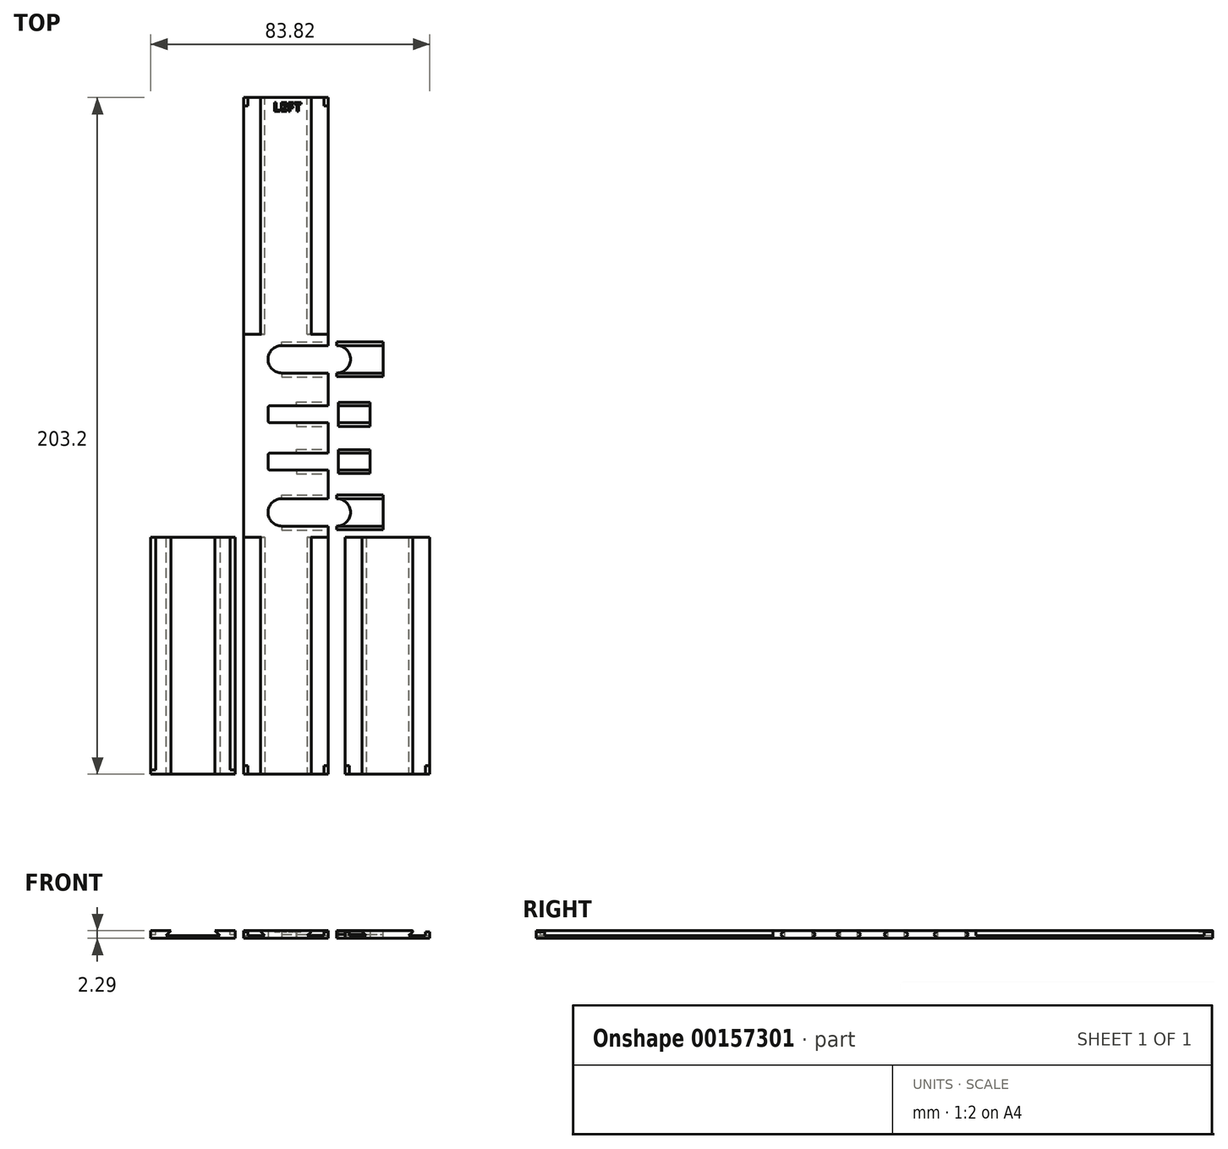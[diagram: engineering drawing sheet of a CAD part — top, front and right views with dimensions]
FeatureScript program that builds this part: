
annotation { "Feature Type Name" : "Feature", "Feature Type Description" : "" }
export const myFeature = defineFeature(function(context is Context, id is Id, definition is map)
    precondition{}
    {
        {
            var Q0;
            Q0=qCreatedBy(makeId("Top.planeOp"),FACE);
            var sketch = newSketch(context, id + "F0", { "sketchPlane" : qUnion([Q0])});
            skLineSegment(sketch, "E0.bottom", {"start": v(-2.54, 205.74) * mm, "end": v(-27.94, 205.74) * mm});
            skLineSegment(sketch, "E0.top", {"start": v(-2.54, 2.54) * mm, "end": v(-27.94, 2.54) * mm});
            skLineSegment(sketch, "E0.left", {"start": v(-2.54, 205.74) * mm, "end": v(-2.54, 131.27) * mm});
            skLineSegment(sketch, "E0.right", {"start": v(-27.94, 205.74) * mm, "end": v(-27.94, 2.54) * mm});
            skLineSegment(sketch, "E1.bottom", {"start": v(-30.48, 2.54) * mm, "end": v(-55.88, 2.54) * mm});
            skLineSegment(sketch, "E1.top", {"start": v(-30.48, 73.66) * mm, "end": v(-55.88, 73.66) * mm});
            skLineSegment(sketch, "E1.left", {"start": v(-30.48, 2.54) * mm, "end": v(-30.48, 73.66) * mm});
            skLineSegment(sketch, "E1.right", {"start": v(-55.88, 2.54) * mm, "end": v(-55.88, 73.66) * mm});
            skLineSegment(sketch, "E2.MirrorCS", {"start": v(2.54, 2.54) * mm, "end": v(2.54, 73.66) * mm});
            skLineSegment(sketch, "E3.MirrorCS", {"start": v(2.54, 73.66) * mm, "end": v(27.94, 73.66) * mm});
            skLineSegment(sketch, "E4.MirrorCS", {"start": v(27.94, 2.54) * mm, "end": v(27.94, 73.66) * mm});
            skLineSegment(sketch, "E5.MirrorCS", {"start": v(2.54, 2.54) * mm, "end": v(27.94, 2.54) * mm});
            skPoint(sketch, "E6.MirrorCS.start.orphan", {"position": v(-30.48, 73.66) * mm});
            skArc(sketch, "E7", {"start": v(-16.51, 131.27) * mm, "mid": v(-20.64, 127.14) * mm, "end": v(-16.51, 123.01) * mm});
            skArc(sketch, "E8", {"start": v(-16.51, 85.3) * mm, "mid": v(-20.64, 81.17) * mm, "end": v(-16.51, 77.04) * mm});
            skLineSegment(sketch, "E9", {"start": v(-16.51, 131.27) * mm, "end": v(-2.54, 131.27) * mm});
            skLineSegment(sketch, "E10", {"start": v(-16.51, 123.01) * mm, "end": v(-2.54, 123.01) * mm});
            skLineSegment(sketch, "E11", {"start": v(-16.51, 85.3) * mm, "end": v(-2.54, 85.3) * mm});
            skLineSegment(sketch, "E12", {"start": v(-16.51, 77.04) * mm, "end": v(-2.54, 77.04) * mm});
            skLineSegment(sketch, "E13.bottom", {"start": v(0, 77.04) * mm, "end": v(13.97, 77.04) * mm});
            skLineSegment(sketch, "E13.top", {"start": v(0, 85.3) * mm, "end": v(13.97, 85.3) * mm});
            skLineSegment(sketch, "E13.right", {"start": v(13.97, 77.04) * mm, "end": v(13.97, 85.3) * mm});
            skLineSegment(sketch, "E14.bottom", {"start": v(0, 123.01) * mm, "end": v(13.97, 123.01) * mm});
            skLineSegment(sketch, "E14.top", {"start": v(0, 131.27) * mm, "end": v(13.97, 131.27) * mm});
            skLineSegment(sketch, "E14.right", {"start": v(13.97, 123.01) * mm, "end": v(13.97, 131.27) * mm});
            skArc(sketch, "E15", {"start": v(0, 77.04) * mm, "mid": v(4.13, 81.17) * mm, "end": v(0, 85.3) * mm});
            skArc(sketch, "E16", {"start": v(0, 123.01) * mm, "mid": v(4.13, 127.14) * mm, "end": v(0, 131.27) * mm});
            skLineSegment(sketch, "E17.bottom", {"start": v(-2.54, 93.87) * mm, "end": v(-20.13, 93.87) * mm});
            skLineSegment(sketch, "E17.top", {"start": v(-2.54, 98.95) * mm, "end": v(-20.13, 98.95) * mm});
            skLineSegment(sketch, "E17.right", {"start": v(-20.64, 94.37) * mm, "end": v(-20.64, 98.44) * mm});
            skLineSegment(sketch, "E18.bottom", {"start": v(-2.54, 108.09) * mm, "end": v(-20.13, 108.09) * mm});
            skLineSegment(sketch, "E18.top", {"start": v(-2.54, 113.17) * mm, "end": v(-20.13, 113.17) * mm});
            skLineSegment(sketch, "E18.right", {"start": v(-20.64, 108.6) * mm, "end": v(-20.64, 112.66) * mm});
            skPoint(sketch, "E19.visualSharp", {"position": v(-20.64, 113.17) * mm});
            skArc(sketch, "E19.filletArc", {"start": v(-20.13, 113.17) * mm, "mid": v(-20.49, 113.02) * mm, "end": v(-20.64, 112.66) * mm});
            skPoint(sketch, "E20.visualSharp", {"position": v(-20.64, 108.09) * mm});
            skArc(sketch, "E20.filletArc", {"start": v(-20.64, 108.6) * mm, "mid": v(-20.49, 108.24) * mm, "end": v(-20.13, 108.09) * mm});
            skPoint(sketch, "E21.visualSharp", {"position": v(-20.64, 98.95) * mm});
            skArc(sketch, "E21.filletArc", {"start": v(-20.13, 98.95) * mm, "mid": v(-20.49, 98.8) * mm, "end": v(-20.64, 98.44) * mm});
            skPoint(sketch, "E22.visualSharp", {"position": v(-20.64, 93.87) * mm});
            skArc(sketch, "E22.filletArc", {"start": v(-20.64, 94.37) * mm, "mid": v(-20.49, 94.01) * mm, "end": v(-20.13, 93.87) * mm});
            skLineSegment(sketch, "E23.bottom", {"start": v(0.42, 113.17) * mm, "end": v(9.95, 113.17) * mm});
            skLineSegment(sketch, "E23.top", {"start": v(0.42, 108.09) * mm, "end": v(9.95, 108.09) * mm});
            skLineSegment(sketch, "E23.left", {"start": v(0.42, 113.17) * mm, "end": v(0.42, 108.09) * mm});
            skLineSegment(sketch, "E23.right", {"start": v(9.95, 113.17) * mm, "end": v(9.95, 108.09) * mm});
            skLineSegment(sketch, "E24.bottom", {"start": v(0.42, 98.95) * mm, "end": v(9.95, 98.95) * mm});
            skLineSegment(sketch, "E24.top", {"start": v(0.42, 93.9) * mm, "end": v(9.95, 93.9) * mm});
            skLineSegment(sketch, "E24.left", {"start": v(0.42, 98.95) * mm, "end": v(0.42, 93.9) * mm});
            skLineSegment(sketch, "E24.right", {"start": v(9.95, 98.95) * mm, "end": v(9.95, 93.9) * mm});
            skLineSegment(sketch, "E25.trimOffspring", {"start": v(-2.54, 77.04) * mm, "end": v(-2.54, 2.54) * mm});
            skLineSegment(sketch, "E26.trimOffspring", {"start": v(-2.54, 123.01) * mm, "end": v(-2.54, 113.17) * mm});
            skLineSegment(sketch, "E27.trimOffspring", {"start": v(-2.54, 108.09) * mm, "end": v(-2.54, 98.95) * mm});
            skLineSegment(sketch, "E28.trimOffspring", {"start": v(-2.54, 93.87) * mm, "end": v(-2.54, 85.3) * mm});
            skSolve(sketch);
        }
        {
            var Q0;
            Q0=qSketchRegion(id+"F0",true);
            extrude(context, id + "F1", {"entities" : qUnion([Q0]), "depth" : 2.3 * mm});
        }
        {
            var Q0;
            Q0=makeQuery(id+"F1.opExtrude","SWEPT_FACE",FACE,{"disambiguationData":[OSD([sQuery(id+"F0.wireOp",EDGE,"E0.top")])]});
            var sketch = newSketch(context, id + "F2", { "sketchPlane" : qUnion([Q0])});
            skLineSegment(sketch, "E29", {"start": v(-22.81, 1.98) * mm, "end": v(-21.59, 0.76) * mm});
            skLineSegment(sketch, "E30", {"start": v(-21.59, 0.76) * mm, "end": v(-27.94, 0.76) * mm});
            skLineSegment(sketch, "E31", {"start": v(-27.94, 0.76) * mm, "end": v(-27.94, 2.29) * mm});
            skLineSegment(sketch, "E32", {"start": v(-8.9, 0.76) * mm, "end": v(-7.67, 1.98) * mm});
            skLineSegment(sketch, "E33", {"start": v(-2.54, 2.29) * mm, "end": v(-2.54, 0.76) * mm});
            skLineSegment(sketch, "E34", {"start": v(-2.54, 0.76) * mm, "end": v(-8.9, 0.76) * mm});
            skPoint(sketch, "E35.visualSharp", {"position": v(-23.11, 2.29) * mm});
            skArc(sketch, "E36.filletArc", {"start": v(-22.68, 2.29) * mm, "mid": v(-22.85, 2.18) * mm, "end": v(-22.81, 1.98) * mm});
            skArc(sketch, "E37.filletArc", {"start": v(-7.67, 1.98) * mm, "mid": v(-7.63, 2.18) * mm, "end": v(-7.8, 2.29) * mm});
            skLineSegment(sketch, "E38", {"start": v(-7.8, 2.29) * mm, "end": v(-2.54, 2.29) * mm});
            skLineSegment(sketch, "E39", {"start": v(-27.94, 2.29) * mm, "end": v(-22.68, 2.29) * mm});
            skLineSegment(sketch, "E40", {"start": v(-49.78, 2.29) * mm, "end": v(-51.3, 0.76) * mm});
            skLineSegment(sketch, "E41", {"start": v(-35.05, 0.76) * mm, "end": v(-36.58, 2.29) * mm});
            skLineSegment(sketch, "E42", {"start": v(-36.58, 2.29) * mm, "end": v(-49.78, 2.29) * mm});
            skLineSegment(sketch, "E43", {"start": v(-51.3, 0.76) * mm, "end": v(-35.05, 0.76) * mm});
            skLineSegment(sketch, "E44.MirrorCS", {"start": v(2.54, 2.29) * mm, "end": v(2.54, 0.76) * mm});
            skLineSegment(sketch, "E45.MirrorCS", {"start": v(2.54, 0.76) * mm, "end": v(8.9, 0.76) * mm});
            skLineSegment(sketch, "E46.MirrorCS", {"start": v(8.9, 0.76) * mm, "end": v(7.67, 1.98) * mm});
            skLineSegment(sketch, "E47.MirrorCS", {"start": v(7.8, 2.29) * mm, "end": v(2.54, 2.29) * mm});
            skArc(sketch, "E48.MirrorCS", {"start": v(7.67, 1.98) * mm, "mid": v(7.63, 2.18) * mm, "end": v(7.8, 2.29) * mm});
            skLineSegment(sketch, "E49.MirrorCS", {"start": v(27.94, 0.76) * mm, "end": v(27.94, 2.29) * mm});
            skLineSegment(sketch, "E50.MirrorCS", {"start": v(27.94, 2.29) * mm, "end": v(22.68, 2.29) * mm});
            skLineSegment(sketch, "E51.MirrorCS", {"start": v(21.59, 0.76) * mm, "end": v(27.94, 0.76) * mm});
            skLineSegment(sketch, "E52.MirrorCS", {"start": v(22.81, 1.98) * mm, "end": v(21.59, 0.76) * mm});
            skArc(sketch, "E53.MirrorCS", {"start": v(22.68, 2.29) * mm, "mid": v(22.85, 2.18) * mm, "end": v(22.81, 1.98) * mm});
            skSolve(sketch);
        }
        {
            var Q0;
            Q0=qSketchRegion(id+"F2",true);
            extrude(context, id + "F3", {"entities" : qUnion([Q0]), "operationType" : NewBodyOperationType.REMOVE, "oppositeDirection" : true, "depth" : 71.12 * mm});
        }
        {
            var Q0;
            Q0=makeQuery(id+"F1.opExtrude","SWEPT_FACE",FACE,{"disambiguationData":[OSD([sQuery(id+"F0.wireOp",EDGE,"E0.bottom")])]});
            var sketch = newSketch(context, id + "F4", { "sketchPlane" : qUnion([Q0])});
            skLineSegment(sketch, "E54", {"start": v(7.67, 1.98) * mm, "end": v(8.9, 0.76) * mm});
            skLineSegment(sketch, "E55", {"start": v(8.9, 0.76) * mm, "end": v(2.54, 0.76) * mm});
            skLineSegment(sketch, "E56", {"start": v(2.54, 0.76) * mm, "end": v(2.54, 2.29) * mm});
            skLineSegment(sketch, "E57", {"start": v(21.59, 0.76) * mm, "end": v(22.81, 1.98) * mm});
            skLineSegment(sketch, "E58", {"start": v(27.94, 2.29) * mm, "end": v(27.94, 0.76) * mm});
            skLineSegment(sketch, "E59", {"start": v(27.94, 0.76) * mm, "end": v(21.59, 0.76) * mm});
            skPoint(sketch, "E60.visualSharp", {"position": v(7.37, 2.28) * mm});
            skArc(sketch, "E61.filletArc", {"start": v(7.8, 2.29) * mm, "mid": v(7.63, 2.18) * mm, "end": v(7.67, 1.98) * mm});
            skArc(sketch, "E62.filletArc", {"start": v(22.81, 1.98) * mm, "mid": v(22.85, 2.18) * mm, "end": v(22.68, 2.29) * mm});
            skLineSegment(sketch, "E63", {"start": v(22.68, 2.29) * mm, "end": v(27.94, 2.29) * mm});
            skLineSegment(sketch, "E64", {"start": v(2.54, 2.29) * mm, "end": v(7.8, 2.29) * mm});
            skSolve(sketch);
        }
        {
            var Q0;
            Q0=qSketchRegion(id+"F4",true);
            extrude(context, id + "F5", {"entities" : qUnion([Q0]), "operationType" : NewBodyOperationType.REMOVE, "oppositeDirection" : true, "depth" : 71.12 * mm});
        }
        {
            var Q0;
            Q0=makeQuery(id+"F3.boolean.opBoolean","COPY",FACE,{"derivedFrom":makeQuery(id+"F3.opExtrude","SWEPT_FACE",FACE,{"disambiguationData":[OSD([sQuery(id+"F2.wireOp",EDGE,"E34")])]})});
            var sketch = newSketch(context, id + "F6", { "sketchPlane" : qUnion([Q0])});
            skLineSegment(sketch, "E65.bottom", {"start": v(-2.54, 2.54) * mm, "end": v(-3.81, 2.54) * mm});
            skLineSegment(sketch, "E65.top", {"start": v(-2.54, 5.08) * mm, "end": v(-3.81, 5.08) * mm});
            skLineSegment(sketch, "E65.left", {"start": v(-2.54, 2.54) * mm, "end": v(-2.54, 5.08) * mm});
            skLineSegment(sketch, "E65.right", {"start": v(-3.81, 2.54) * mm, "end": v(-3.81, 5.08) * mm});
            skLineSegment(sketch, "E66.bottom", {"start": v(-26.67, 2.54) * mm, "end": v(-27.94, 2.54) * mm});
            skLineSegment(sketch, "E66.top", {"start": v(-26.67, 5.08) * mm, "end": v(-27.94, 5.08) * mm});
            skLineSegment(sketch, "E66.left", {"start": v(-26.67, 2.54) * mm, "end": v(-26.67, 5.08) * mm});
            skLineSegment(sketch, "E66.right", {"start": v(-27.94, 2.54) * mm, "end": v(-27.94, 5.08) * mm});
            skLineSegment(sketch, "E67.bottom", {"start": v(27.94, 2.54) * mm, "end": v(26.67, 2.54) * mm});
            skLineSegment(sketch, "E67.top", {"start": v(27.94, 5.08) * mm, "end": v(26.67, 5.08) * mm});
            skLineSegment(sketch, "E67.left", {"start": v(27.94, 2.54) * mm, "end": v(27.94, 5.08) * mm});
            skLineSegment(sketch, "E67.right", {"start": v(26.67, 2.54) * mm, "end": v(26.67, 5.08) * mm});
            skLineSegment(sketch, "E68.bottom", {"start": v(3.81, 2.54) * mm, "end": v(2.54, 2.54) * mm});
            skLineSegment(sketch, "E68.top", {"start": v(3.81, 5.08) * mm, "end": v(2.54, 5.08) * mm});
            skLineSegment(sketch, "E68.left", {"start": v(3.81, 2.54) * mm, "end": v(3.81, 5.08) * mm});
            skLineSegment(sketch, "E68.right", {"start": v(2.54, 2.54) * mm, "end": v(2.54, 5.08) * mm});
            skLineSegment(sketch, "E69.bottom", {"start": v(-27.94, 205.74) * mm, "end": v(-26.67, 205.74) * mm});
            skLineSegment(sketch, "E69.top", {"start": v(-27.94, 203.2) * mm, "end": v(-26.67, 203.2) * mm});
            skLineSegment(sketch, "E69.left", {"start": v(-27.94, 205.74) * mm, "end": v(-27.94, 203.2) * mm});
            skLineSegment(sketch, "E69.right", {"start": v(-26.67, 205.74) * mm, "end": v(-26.67, 203.2) * mm});
            skLineSegment(sketch, "E70.bottom", {"start": v(-3.8, 205.74) * mm, "end": v(-2.54, 205.74) * mm});
            skLineSegment(sketch, "E70.top", {"start": v(-3.8, 203.2) * mm, "end": v(-2.54, 203.2) * mm});
            skLineSegment(sketch, "E70.left", {"start": v(-3.8, 205.74) * mm, "end": v(-3.8, 203.2) * mm});
            skLineSegment(sketch, "E70.right", {"start": v(-2.54, 205.74) * mm, "end": v(-2.54, 203.2) * mm});
            skSolve(sketch);
        }
        {
            var Q0;
            Q0=qSketchRegion(id+"F6",true);
            extrude(context, id + "F7", {"entities" : qUnion([Q0]), "operationType" : NewBodyOperationType.ADD, "depth" : 1.14 * mm});
        }
        {
            var Q0;
            {var subQ0=sQuery(id+"F0.wireOp",EDGE,"E1.bottom");var subQ1=sQuery(id+"F0.wireOp",EDGE,"E1.top");var subQ2=sQuery(id+"F0.wireOp",EDGE,"E1.right");Q0=makeQuery(id+"F3.boolean.opBoolean","SPLIT",FACE,{"disambiguationData":[TD([makeQuery(id+"F1.opExtrude","SWEPT_FACE",FACE,{"disambiguationData":[OSD([subQ2])]})])],"derivedFrom":makeQuery(id+"F1.opExtrude","CAP_FACE",FACE,{"disambiguationData":[OSD([subQ0,subQ1,sQuery(id+"F0.wireOp",EDGE,"E1.left"),subQ2])],"isStart":false})});}
            var sketch = newSketch(context, id + "F8", { "sketchPlane" : qUnion([Q0])});
            skLineSegment(sketch, "E71.bottom", {"start": v(-30.48, 3.8) * mm, "end": v(-32, 3.8) * mm});
            skLineSegment(sketch, "E71.top", {"start": v(-30.48, 73.66) * mm, "end": v(-32, 73.66) * mm});
            skLineSegment(sketch, "E71.left", {"start": v(-30.48, 3.8) * mm, "end": v(-30.48, 73.66) * mm});
            skLineSegment(sketch, "E71.right", {"start": v(-32, 3.8) * mm, "end": v(-32, 73.66) * mm});
            skLineSegment(sketch, "E72.bottom", {"start": v(-54.36, 3.8) * mm, "end": v(-55.88, 3.8) * mm});
            skLineSegment(sketch, "E72.top", {"start": v(-54.36, 73.66) * mm, "end": v(-55.88, 73.66) * mm});
            skLineSegment(sketch, "E72.left", {"start": v(-54.36, 3.8) * mm, "end": v(-54.36, 73.66) * mm});
            skLineSegment(sketch, "E72.right", {"start": v(-55.88, 3.8) * mm, "end": v(-55.88, 73.66) * mm});
            skSolve(sketch);
        }
        {
            var Q0;
            Q0=qSketchRegion(id+"F8",true);
            extrude(context, id + "F9", {"entities" : qUnion([Q0]), "operationType" : NewBodyOperationType.REMOVE, "oppositeDirection" : true, "depth" : 1.27 * mm});
        }
        {
            var Q0;
            Q0=makeQuery(id+"F1.opExtrude","SWEPT_FACE",FACE,{"disambiguationData":[OSD([sQuery(id+"F0.wireOp",EDGE,"E28.trimOffspring")])]});
            var sketch = newSketch(context, id + "F10", { "sketchPlane" : qUnion([Q0])});
            skLineSegment(sketch, "E73", {"start": v(85.3, 2.29) * mm, "end": v(86.44, 1.14) * mm});
            skLineSegment(sketch, "E74", {"start": v(86.44, 1.14) * mm, "end": v(85.3, 0) * mm});
            skLineSegment(sketch, "E75", {"start": v(123.01, 2.29) * mm, "end": v(121.87, 1.14) * mm});
            skLineSegment(sketch, "E76", {"start": v(121.87, 1.14) * mm, "end": v(123.01, 0) * mm});
            skLineSegment(sketch, "E77", {"start": v(123.01, 0) * mm, "end": v(123.01, 2.29) * mm});
            skLineSegment(sketch, "E78", {"start": v(131.27, 2.29) * mm, "end": v(132.41, 1.14) * mm});
            skLineSegment(sketch, "E79", {"start": v(132.41, 1.14) * mm, "end": v(131.27, 0) * mm});
            skLineSegment(sketch, "E80", {"start": v(131.27, 0) * mm, "end": v(131.27, 2.29) * mm});
            skLineSegment(sketch, "E81", {"start": v(85.3, 2.29) * mm, "end": v(85.3, 0) * mm});
            skLineSegment(sketch, "E82", {"start": v(77.04, 2.29) * mm, "end": v(75.9, 1.14) * mm});
            skLineSegment(sketch, "E83", {"start": v(75.9, 1.14) * mm, "end": v(77.04, 0) * mm});
            skLineSegment(sketch, "E84", {"start": v(77.04, 0) * mm, "end": v(77.04, 2.29) * mm});
            skSolve(sketch);
        }
        {
            var Q0;
            Q0=qSketchRegion(id+"F10",true);
            extrude(context, id + "F11", {"entities" : qUnion([Q0]), "operationType" : NewBodyOperationType.REMOVE, "oppositeDirection" : true, "depth" : 13.97 * mm});
        }
        {
            var Q0;
            Q0=makeQuery(id+"F1.opExtrude","SWEPT_FACE",FACE,{"disambiguationData":[OSD([sQuery(id+"F0.wireOp",EDGE,"E13.right")])]});
            var sketch = newSketch(context, id + "F12", { "sketchPlane" : qUnion([Q0])});
            skLineSegment(sketch, "E85", {"start": v(77.04, 2.2) * mm, "end": v(75.97, 1.14) * mm});
            skLineSegment(sketch, "E86", {"start": v(75.97, 1.14) * mm, "end": v(77.04, 0.08) * mm});
            skLineSegment(sketch, "E87", {"start": v(77.04, 0.08) * mm, "end": v(77.04, 2.2) * mm});
            skLineSegment(sketch, "E88", {"start": v(85.3, 0.08) * mm, "end": v(86.36, 1.14) * mm});
            skLineSegment(sketch, "E89", {"start": v(86.36, 1.14) * mm, "end": v(85.3, 2.2) * mm});
            skLineSegment(sketch, "E90", {"start": v(85.3, 2.2) * mm, "end": v(85.3, 0.08) * mm});
            skLineSegment(sketch, "E91", {"start": v(123.01, 2.2) * mm, "end": v(121.95, 1.14) * mm});
            skLineSegment(sketch, "E92", {"start": v(121.95, 1.14) * mm, "end": v(123.01, 0.08) * mm});
            skLineSegment(sketch, "E93", {"start": v(123.01, 0.08) * mm, "end": v(123.01, 2.2) * mm});
            skLineSegment(sketch, "E94", {"start": v(131.27, 0.08) * mm, "end": v(132.33, 1.14) * mm});
            skLineSegment(sketch, "E95", {"start": v(132.33, 1.14) * mm, "end": v(131.27, 2.2) * mm});
            skLineSegment(sketch, "E96", {"start": v(131.27, 2.2) * mm, "end": v(131.27, 0.08) * mm});
            skSolve(sketch);
        }
        {
            var Q0;
            Q0=qSketchRegion(id+"F12",true);
            extrude(context, id + "F13", {"entities" : qUnion([Q0]), "operationType" : NewBodyOperationType.ADD, "oppositeDirection" : true, "depth" : 13.97 * mm});
        }
        {
            var Q0;
            Q0=makeQuery(id+"F1.opExtrude","SWEPT_FACE",FACE,{"disambiguationData":[OSD([sQuery(id+"F0.wireOp",EDGE,"E24.right")])]});
            var sketch = newSketch(context, id + "F14", { "sketchPlane" : qUnion([Q0])});
            skLineSegment(sketch, "E97", {"start": v(93.9, 2.24) * mm, "end": v(92.82, 1.14) * mm});
            skLineSegment(sketch, "E98", {"start": v(92.82, 1.14) * mm, "end": v(93.9, 0.05) * mm});
            skLineSegment(sketch, "E99", {"start": v(93.9, 0.05) * mm, "end": v(93.9, 2.24) * mm});
            skLineSegment(sketch, "E100", {"start": v(98.95, 2.24) * mm, "end": v(100.04, 1.14) * mm});
            skLineSegment(sketch, "E101", {"start": v(100.04, 1.14) * mm, "end": v(98.95, 0.05) * mm});
            skLineSegment(sketch, "E102", {"start": v(98.95, 0.05) * mm, "end": v(98.95, 2.24) * mm});
            skLineSegment(sketch, "E103", {"start": v(108.09, 2.24) * mm, "end": v(107, 1.14) * mm});
            skLineSegment(sketch, "E104", {"start": v(107, 1.14) * mm, "end": v(108.09, 0.05) * mm});
            skLineSegment(sketch, "E105", {"start": v(108.09, 0.05) * mm, "end": v(108.09, 2.24) * mm});
            skLineSegment(sketch, "E106", {"start": v(113.17, 2.24) * mm, "end": v(114.26, 1.14) * mm});
            skLineSegment(sketch, "E107", {"start": v(114.26, 1.14) * mm, "end": v(113.17, 0.05) * mm});
            skLineSegment(sketch, "E108", {"start": v(113.17, 0.05) * mm, "end": v(113.17, 2.24) * mm});
            skSolve(sketch);
        }
        {
            var Q0;
            Q0=makeQuery(id+"F1.opExtrude","SWEPT_FACE",FACE,{"disambiguationData":[OSD([sQuery(id+"F0.wireOp",EDGE,"E27.trimOffspring")])]});
            var sketch = newSketch(context, id + "F15", { "sketchPlane" : qUnion([Q0])});
            skLineSegment(sketch, "E109", {"start": v(93.87, 2.29) * mm, "end": v(92.72, 1.14) * mm});
            skLineSegment(sketch, "E110", {"start": v(92.72, 1.14) * mm, "end": v(93.87, 0) * mm});
            skLineSegment(sketch, "E111", {"start": v(93.87, 0) * mm, "end": v(93.87, 2.29) * mm});
            skLineSegment(sketch, "E112", {"start": v(98.95, 2.29) * mm, "end": v(100.09, 1.14) * mm});
            skLineSegment(sketch, "E113", {"start": v(100.09, 1.14) * mm, "end": v(98.95, 0) * mm});
            skLineSegment(sketch, "E114", {"start": v(98.95, 0) * mm, "end": v(98.95, 2.29) * mm});
            skLineSegment(sketch, "E115", {"start": v(113.17, 2.29) * mm, "end": v(114.31, 1.14) * mm});
            skLineSegment(sketch, "E116", {"start": v(114.31, 1.14) * mm, "end": v(113.17, 0) * mm});
            skLineSegment(sketch, "E117", {"start": v(113.17, 0) * mm, "end": v(113.17, 2.29) * mm});
            skLineSegment(sketch, "E118", {"start": v(108.09, 2.29) * mm, "end": v(106.95, 1.14) * mm});
            skLineSegment(sketch, "E119", {"start": v(106.95, 1.14) * mm, "end": v(108.09, 0) * mm});
            skLineSegment(sketch, "E120", {"start": v(108.09, 0) * mm, "end": v(108.09, 2.29) * mm});
            skSolve(sketch);
        }
        {
            var Q0;
            Q0=qSketchRegion(id+"F15",true);
            extrude(context, id + "F16", {"entities" : qUnion([Q0]), "operationType" : NewBodyOperationType.REMOVE, "oppositeDirection" : true, "depth" : 9.52 * mm});
        }
        {
            var Q0;
            Q0=qSketchRegion(id+"F14",true);
            extrude(context, id + "F17", {"entities" : qUnion([Q0]), "operationType" : NewBodyOperationType.ADD, "oppositeDirection" : true, "depth" : 9.52 * mm});
        }
        {
            var Q0;
            Q0=makeQuery(id+"F1.opExtrude","CAP_FACE",FACE,{"disambiguationData":[OSD([sQuery(id+"F0.wireOp",EDGE,"E0.bottom"),sQuery(id+"F0.wireOp",EDGE,"E0.top"),sQuery(id+"F0.wireOp",EDGE,"E0.left"),sQuery(id+"F0.wireOp",EDGE,"E0.right"),sQuery(id+"F0.wireOp",EDGE,"E7"),sQuery(id+"F0.wireOp",EDGE,"E8"),sQuery(id+"F0.wireOp",EDGE,"E9"),sQuery(id+"F0.wireOp",EDGE,"E10"),sQuery(id+"F0.wireOp",EDGE,"E11"),sQuery(id+"F0.wireOp",EDGE,"E12"),sQuery(id+"F0.wireOp",EDGE,"E17.bottom"),sQuery(id+"F0.wireOp",EDGE,"E17.top"),sQuery(id+"F0.wireOp",EDGE,"E17.right"),sQuery(id+"F0.wireOp",EDGE,"E18.bottom"),sQuery(id+"F0.wireOp",EDGE,"E18.top"),sQuery(id+"F0.wireOp",EDGE,"E18.right"),sQuery(id+"F0.wireOp",EDGE,"E19.filletArc"),sQuery(id+"F0.wireOp",EDGE,"E20.filletArc"),sQuery(id+"F0.wireOp",EDGE,"E21.filletArc"),sQuery(id+"F0.wireOp",EDGE,"E22.filletArc"),sQuery(id+"F0.wireOp",EDGE,"E25.trimOffspring"),sQuery(id+"F0.wireOp",EDGE,"E26.trimOffspring"),sQuery(id+"F0.wireOp",EDGE,"E27.trimOffspring"),sQuery(id+"F0.wireOp",EDGE,"E28.trimOffspring")])],"isStart":false});
            var sketch = newSketch(context, id + "F18", { "sketchPlane" : qUnion([Q0])});
            skText(sketch, "E121", { "text": "LEFT", "fontName": "OpenSans-Bold.ttf"});
            const initialGuessF18  = {"E121": [-0.01908, 0.20155, 1, 0, 0.0027]};
            skSetInitialGuess(sketch, initialGuessF18);
            skSolve(sketch);
        }
        {
            var Q0;
            Q0=qSketchRegion(id+"F18",true);
            extrude(context, id + "F19", {"entities" : qUnion([Q0]), "operationType" : NewBodyOperationType.REMOVE, "oppositeDirection" : true, "depth" : 0.38 * mm});
        }
    });
